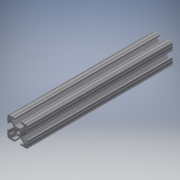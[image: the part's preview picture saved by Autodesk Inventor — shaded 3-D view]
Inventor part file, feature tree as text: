
AUTODESK INVENTOR PART (.ipt)
format: ipt  version: 2018 (Build 220112000, 112)  size: 226,304 bytes
history: native  units: in
note: dims shown in document units (in); Inventor stores cm internally (conversion verified against a paired STEP export)
features: extrude x1, sketch x1
ambient origin geometry x8: Origin, YZ Plane, XZ Plane, XY Plane, X Axis, Y Axis, Z Axis, Center Point
bodies: Solid1 (feature_tree)
feature tree (2):
  extrude  "Extrusion1"  [1 undecoded]
  sketch  "Sketch1"  dims[d0=7.0in d1=0.0in]
note: 1 required parameter value undecoded (feature->parameter linkage not recoverable at this tier; creation-order binding heuristic only, values carry confidence <= 0.55)
